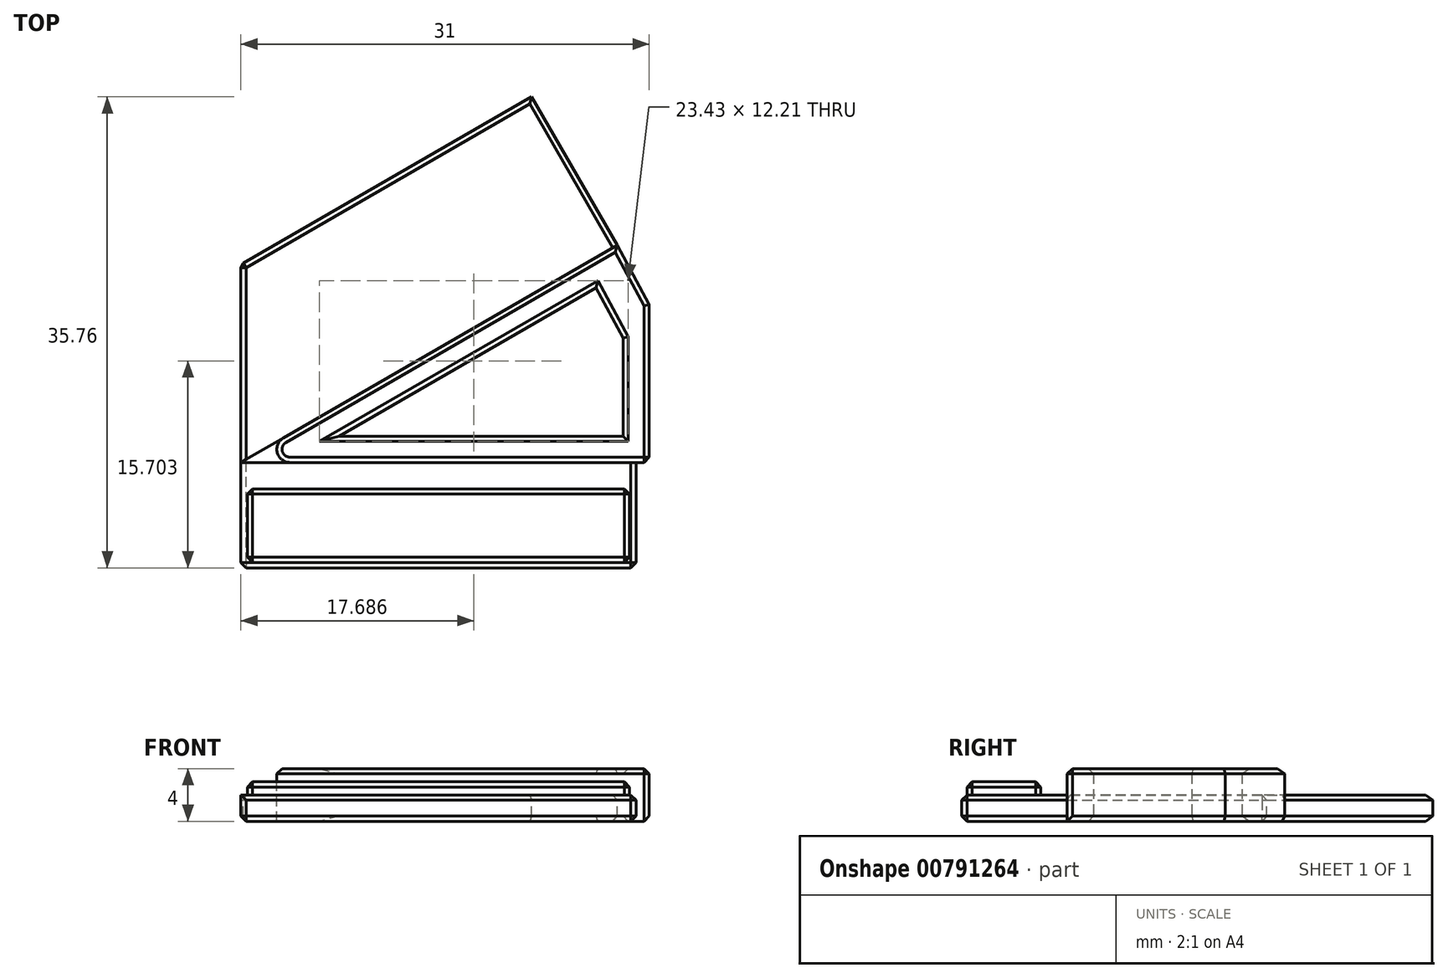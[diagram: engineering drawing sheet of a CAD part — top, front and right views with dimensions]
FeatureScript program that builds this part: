
annotation { "Feature Type Name" : "Feature", "Feature Type Description" : "" }
export const myFeature = defineFeature(function(context is Context, id is Id, definition is map)
    precondition{}
    {
        {
            var Q0;
            Q0=qCreatedBy(makeId("Top.planeOp"),FACE);
            var sketch = newSketch(context, id + "F0", { "sketchPlane" : qUnion([Q0])});
            skLineSegment(sketch, "E0", {"start": v(0, 0) * mm, "end": v(31, 0) * mm});
            skLineSegment(sketch, "E1", {"start": v(0, 0) * mm, "end": v(28.58, 16.5) * mm});
            skLineSegment(sketch, "E2", {"start": v(31, 0) * mm, "end": v(31, 12) * mm});
            skLineSegment(sketch, "E3", {"start": v(31, 12) * mm, "end": v(28.58, 16.5) * mm});
            skLineSegment(sketch, "E4", {"start": v(7.46, 2) * mm, "end": v(29, 2) * mm});
            skLineSegment(sketch, "E5", {"start": v(7.46, 2) * mm, "end": v(26.96, 13.25) * mm});
            skLineSegment(sketch, "E6", {"start": v(29, 2) * mm, "end": v(29, 9.45) * mm});
            skLineSegment(sketch, "E7", {"start": v(26.96, 13.25) * mm, "end": v(29, 9.45) * mm});
            skSolve(sketch);
        }
        {
            var Q0;
            Q0=makeQuery(id+"F0.imprint","IMPRINT",FACE,{"disambiguationData":[TD([[makeQuery(id+"F0.imprint","IMPRINT",EDGE,{"derivedFrom":sQuery(id+"F0.wireOp",EDGE,"E0")}),1.0]])]});
            extrude(context, id + "F1", {"entities" : qUnion([Q0]), "endBound" : BoundingType.SYMMETRIC, "depth" : 4 * mm, "offsetDistance" : 25 * mm});
        }
        {
            var Q0;
            Q0=qCreatedBy(makeId("Top.planeOp"),FACE);
            var sketch = newSketch(context, id + "F2", { "sketchPlane" : qUnion([Q0])});
            skLineSegment(sketch, "E8.bottom", {"start": v(0, 0) * mm, "end": v(30, 0) * mm});
            skLineSegment(sketch, "E8.top", {"start": v(0, -8) * mm, "end": v(30, -8) * mm});
            skLineSegment(sketch, "E8.left", {"start": v(0, 0) * mm, "end": v(0, -8) * mm});
            skLineSegment(sketch, "E8.right", {"start": v(30, 0) * mm, "end": v(30, -8) * mm});
            skLineSegment(sketch, "E9", {"start": v(0, 0) * mm, "end": v(28.58, 16.5) * mm});
            skLineSegment(sketch, "E10", {"start": v(28.58, 16.5) * mm, "end": v(22.08, 27.76) * mm});
            skLineSegment(sketch, "E11", {"start": v(22.08, 27.76) * mm, "end": v(0, 15.01) * mm});
            skLineSegment(sketch, "E12.MirrorCS", {"start": v(0, 15.01) * mm, "end": v(0, 0) * mm});
            skLineSegment(sketch, "E13.bottom", {"start": v(0.5, -2) * mm, "end": v(29.5, -2) * mm});
            skLineSegment(sketch, "E13.top", {"start": v(0.5, -7.6) * mm, "end": v(29.5, -7.6) * mm});
            skLineSegment(sketch, "E13.left", {"start": v(0.5, -2) * mm, "end": v(0.5, -7.6) * mm});
            skLineSegment(sketch, "E13.right", {"start": v(29.5, -2) * mm, "end": v(29.5, -7.6) * mm});
            skSolve(sketch);
        }
        {
            var Q0;
            Q0=makeQuery(id+"F2.imprint","IMPRINT",FACE,{"disambiguationData":[TD([[makeQuery(id+"F2.imprint","IMPRINT",EDGE,{"derivedFrom":sQuery(id+"F2.wireOp",EDGE,"E8.bottom")}),-1.0]])]});
            var Q1;
            {var subQ1=sQuery(id+"F2.wireOp",EDGE,"E9");Q1=makeQuery(id+"F2.imprint","IMPRINT",FACE,{"disambiguationData":[TD([[makeQuery(id+"F2.imprint","IMPRINT",EDGE,{"derivedFrom":subQ1}),1.0]])]});}
            extrude(context, id + "F3", {"entities" : qUnion([Q0, Q1]), "oppositeDirection" : true, "depth" : 2 * mm, "offsetDistance" : 25 * mm});
        }
        {
            var Q0;
            Q0=makeQuery(id+"F1.opExtrude","SWEPT_EDGE",EDGE,{"disambiguationData":[OSD([sQuery(id+"F0.wireOp",EDGE,"E0"),sQuery(id+"F0.wireOp",EDGE,"E1")])]});
            fillet(context, id + "F4", {"entities" : qUnion([Q0]), "radius" : 1 * mm, "tangentPropagation" : true, "allowEdgeOverflow" : false});
        }
        {
            var Q0;
            Q0=makeQuery(id+"F2.imprint","IMPRINT",FACE,{"disambiguationData":[TD([[makeQuery(id+"F2.imprint","IMPRINT",EDGE,{"derivedFrom":sQuery(id+"F2.wireOp",EDGE,"E13.bottom")}),-1.0]])]});
            extrude(context, id + "F5", {"entities" : qUnion([Q0]), "operationType" : NewBodyOperationType.ADD, "depth" : 1 * mm, "offsetDistance" : 25 * mm, "hasSecondDirection" : true, "secondDirectionOppositeDirection" : true, "secondDirectionDepth" : 2 * mm});
        }
        {
            var Q0;
            Q0=makeQuery(id+"F3.opExtrude","CAP_EDGE",EDGE,{"disambiguationData":[OSD([sQuery(id+"F2.wireOp",EDGE,"E11")])],"isStart":true});
            var Q1;
            Q1=makeQuery(id+"F3.opExtrude","CAP_EDGE",EDGE,{"disambiguationData":[OSD([sQuery(id+"F2.wireOp",EDGE,"E11")])],"isStart":false});
            var Q2;
            Q2=makeQuery(id+"F3.opExtrude","SWEPT_EDGE",EDGE,{"disambiguationData":[OSD([sQuery(id+"F2.wireOp",EDGE,"E11"),sQuery(id+"F2.wireOp",EDGE,"E12.MirrorCS")])]});
            var Q3;
            Q3=makeQuery(id+"F3.opExtrude","CAP_EDGE",EDGE,{"disambiguationData":[OSD([sQuery(id+"F2.wireOp",EDGE,"E12.MirrorCS")])],"isStart":true});
            var Q4;
            Q4=makeQuery(id+"F3.opExtrude","CAP_EDGE",EDGE,{"disambiguationData":[OSD([sQuery(id+"F2.wireOp",EDGE,"E12.MirrorCS")])],"isStart":false});
            var Q5;
            Q5=makeQuery(id+"F5.opExtrude","CAP_EDGE",EDGE,{"disambiguationData":[OSD([sQuery(id+"F2.wireOp",EDGE,"E13.left")])],"isStart":false});
            var Q6;
            Q6=makeQuery(id+"F5.opExtrude","CAP_EDGE",EDGE,{"disambiguationData":[OSD([sQuery(id+"F2.wireOp",EDGE,"E13.bottom")])],"isStart":false});
            var Q7;
            Q7=makeQuery(id+"F5.opExtrude","CAP_EDGE",EDGE,{"disambiguationData":[OSD([sQuery(id+"F2.wireOp",EDGE,"E13.right")])],"isStart":false});
            var Q8;
            Q8=makeQuery(id+"F5.opExtrude","CAP_EDGE",EDGE,{"disambiguationData":[OSD([sQuery(id+"F2.wireOp",EDGE,"E13.top")])],"isStart":false});
            var Q9;
            Q9=makeQuery(id+"F3.opExtrude","CAP_EDGE",EDGE,{"disambiguationData":[OSD([sQuery(id+"F2.wireOp",EDGE,"E8.left")])],"isStart":false});
            var Q10;
            Q10=makeQuery(id+"F3.opExtrude","SWEPT_EDGE",EDGE,{"disambiguationData":[OSD([sQuery(id+"F2.wireOp",EDGE,"E8.top"),sQuery(id+"F2.wireOp",EDGE,"E8.left")])]});
            var Q11;
            Q11=makeQuery(id+"F3.opExtrude","CAP_EDGE",EDGE,{"disambiguationData":[OSD([sQuery(id+"F2.wireOp",EDGE,"E10")])],"isStart":true});
            var Q12;
            Q12=makeQuery(id+"F3.opExtrude","CAP_EDGE",EDGE,{"disambiguationData":[OSD([sQuery(id+"F2.wireOp",EDGE,"E10")])],"isStart":false});
            var Q13;
            Q13=makeQuery(id+"F1.opExtrude","CAP_EDGE",EDGE,{"disambiguationData":[OSD([sQuery(id+"F0.wireOp",EDGE,"E3")])],"isStart":true});
            var Q14;
            Q14=makeQuery(id+"F1.opExtrude","CAP_EDGE",EDGE,{"disambiguationData":[OSD([sQuery(id+"F0.wireOp",EDGE,"E2")])],"isStart":true});
            var Q15;
            Q15=makeQuery(id+"F3.opExtrude","CAP_EDGE",EDGE,{"disambiguationData":[OSD([sQuery(id+"F2.wireOp",EDGE,"E8.right")])],"isStart":false});
            var Q16;
            Q16=makeQuery(id+"F3.opExtrude","SWEPT_EDGE",EDGE,{"disambiguationData":[OSD([sQuery(id+"F2.wireOp",EDGE,"E8.top"),sQuery(id+"F2.wireOp",EDGE,"E8.right")])]});
            var Q17;
            Q17=makeQuery(id+"F3.opExtrude","CAP_EDGE",EDGE,{"disambiguationData":[OSD([sQuery(id+"F2.wireOp",EDGE,"E8.top")])],"isStart":false});
            var Q18;
            Q18=makeQuery(id+"F1.opExtrude","CAP_EDGE",EDGE,{"disambiguationData":[OSD([sQuery(id+"F0.wireOp",EDGE,"E1")])],"isStart":false});
            var Q19;
            Q19=makeQuery(id+"F1.opExtrude","CAP_EDGE",EDGE,{"disambiguationData":[OSD([sQuery(id+"F0.wireOp",EDGE,"E3")])],"isStart":false});
            var Q20;
            Q20=makeQuery(id+"F1.opExtrude","CAP_EDGE",EDGE,{"disambiguationData":[OSD([sQuery(id+"F0.wireOp",EDGE,"E2")])],"isStart":false});
            var Q21;
            Q21=makeQuery(id+"F1.opExtrude","CAP_EDGE",EDGE,{"disambiguationData":[OSD([sQuery(id+"F0.wireOp",EDGE,"E5")])],"isStart":false});
            var Q22;
            Q22=makeQuery(id+"F1.opExtrude","CAP_EDGE",EDGE,{"disambiguationData":[OSD([sQuery(id+"F0.wireOp",EDGE,"E4")])],"isStart":false});
            var Q23;
            Q23=makeQuery(id+"F1.opExtrude","CAP_EDGE",EDGE,{"disambiguationData":[OSD([sQuery(id+"F0.wireOp",EDGE,"E6")])],"isStart":false});
            var Q24;
            Q24=makeQuery(id+"F1.opExtrude","CAP_EDGE",EDGE,{"disambiguationData":[OSD([sQuery(id+"F0.wireOp",EDGE,"E7")])],"isStart":false});
            var Q25;
            Q25=makeQuery(id+"F1.opExtrude","CAP_EDGE",EDGE,{"disambiguationData":[OSD([sQuery(id+"F0.wireOp",EDGE,"E4")])],"isStart":true});
            var Q26;
            Q26=makeQuery(id+"F1.opExtrude","CAP_EDGE",EDGE,{"disambiguationData":[OSD([sQuery(id+"F0.wireOp",EDGE,"E6")])],"isStart":true});
            var Q27;
            Q27=makeQuery(id+"F1.opExtrude","CAP_EDGE",EDGE,{"disambiguationData":[OSD([sQuery(id+"F0.wireOp",EDGE,"E7")])],"isStart":true});
            var Q28;
            Q28=makeQuery(id+"F1.opExtrude","CAP_EDGE",EDGE,{"disambiguationData":[OSD([sQuery(id+"F0.wireOp",EDGE,"E5")])],"isStart":true});
            var Q29;
            Q29=makeQuery(id+"F5.opExtrude","SWEPT_EDGE",EDGE,{"disambiguationData":[OSD([sQuery(id+"F2.wireOp",EDGE,"E13.bottom"),sQuery(id+"F2.wireOp",EDGE,"E13.left")])]});
            var Q30;
            Q30=makeQuery(id+"F5.opExtrude","SWEPT_EDGE",EDGE,{"disambiguationData":[OSD([sQuery(id+"F2.wireOp",EDGE,"E13.top"),sQuery(id+"F2.wireOp",EDGE,"E13.left")])]});
            var Q31;
            Q31=makeQuery(id+"F5.opExtrude","SWEPT_EDGE",EDGE,{"disambiguationData":[OSD([sQuery(id+"F2.wireOp",EDGE,"E13.top"),sQuery(id+"F2.wireOp",EDGE,"E13.right")])]});
            var Q32;
            Q32=makeQuery(id+"F5.opExtrude","SWEPT_EDGE",EDGE,{"disambiguationData":[OSD([sQuery(id+"F2.wireOp",EDGE,"E13.bottom"),sQuery(id+"F2.wireOp",EDGE,"E13.right")])]});
            var Q33;
            Q33=makeQuery(id+"F3.opExtrude","CAP_EDGE",EDGE,{"disambiguationData":[OSD([sQuery(id+"F2.wireOp",EDGE,"E8.right")])],"isStart":true});
            var Q34;
            Q34=makeQuery(id+"F1.opExtrude","SWEPT_EDGE",EDGE,{"disambiguationData":[OSD([sQuery(id+"F0.wireOp",EDGE,"E0"),sQuery(id+"F0.wireOp",EDGE,"E2")])]});
            var Q35;
            Q35=makeQuery(id+"F3.opExtrude","CAP_EDGE",EDGE,{"disambiguationData":[OSD([sQuery(id+"F2.wireOp",EDGE,"E8.top")])],"isStart":true});
            chamfer(context, id + "F6", {"entities" : qUnion([Q0, Q1, Q2, Q3, Q4, Q5, Q6, Q7, Q8, Q9, Q10, Q11, Q12, Q13, Q14, Q15, Q16, Q17, Q18, Q19, Q20, Q21, Q22, Q23, Q24, Q25, Q26, Q27, Q28, Q29, Q30, Q31, Q32, Q33, Q34, Q35]), "width" : .4 * mm, "tangentPropagation" : true});
        }
    });
